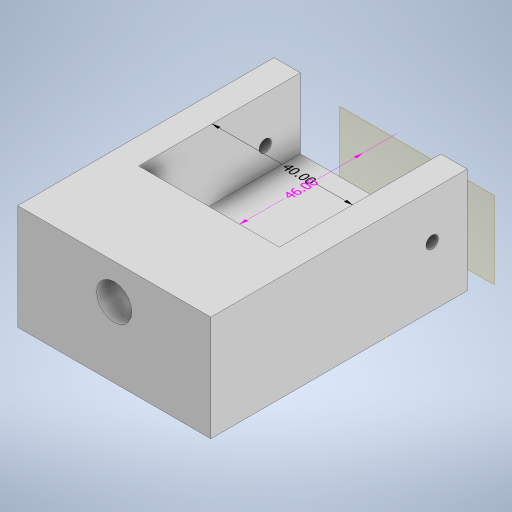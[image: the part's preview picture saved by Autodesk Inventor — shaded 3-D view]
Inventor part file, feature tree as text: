
AUTODESK INVENTOR PART (.ipt)
format: ipt  version: 2023 (Build 270158000, 158)  size: 300,544 bytes
history: native  units: mm
features: sketch x8, extrude x6, other x4, plane x3, hole x1, split x1
ambient origin geometry x8: Origin, YZ Plane, XZ Plane, XY Plane, X Axis, Y Axis, Z Axis, Center Point
bodies: Body1 (feature_tree)
feature tree (23):
  other  "Sólido1"
  other  "Anotaciones"
  extrude  "Extrusión1"  Depth=55.0mm
  extrude  "Extrusión2"  Depth=10.0mm
  extrude  "Extrusión3"  Depth=5.0mm
  extrude  "Extrusión4"  Depth=10.0mm TaperAngle=0.0deg
  plane  "Plano de trabajo1"
  extrude  "Extrusión5"  Depth=10.0mm
  plane  "Plano de trabajo2"
  extrude  "Extrusión6"  Depth=40.0mm
  sketch  "Boceto7"  dims[d15=46.0mm d16=20.0mm d17=0.0mm]
  plane  "Plano de trabajo4"
  hole  "Agujero1"  [1 undecoded]
  split  "Dividir1"
  sketch  "Boceto1"  dims[d0=55.0mm d1=100.0mm]
  sketch  "Boceto2"  dims[d2=30.0mm d3=0.0mm d4=10.0mm]
  sketch  "Boceto3"  dims[d5=20.0mm d6=5.0mm]
  sketch  "Boceto4"  dims[d7=22.5mm d8=10.0mm d9=0.0mm]
  sketch  "Boceto5"  dims[d10=10.0mm d11=10.0mm]
  sketch  "Boceto6"  dims[d12=15.0mm d13=0.0mm d14=40.0mm]
  sketch  "Boceto8"  dims[d24=22.5mm d25=2.5mm d26=2.5mm d27=8.0mm d28=0.0mm d29=3.0mm d30=3.0mm d31=8.0mm d32=0.0mm d33=0.0mm d34=10.0mm d35=30.0mm d36=5.0mm d37=5.0mm d38=5.0mm d39=5.0mm d40=10.0mm d41=8.0mm d42=3.5mm d43=6.0mm d44=4.0mm d45=2.0mm d46=90.0deg d47=8.0mm d48=20.594885mm d18=5.462798mm d19=4.90751mm d20=46.0mm d21=4.68859mm d22=6.124374mm d23=40.0mm]
  other  "Cota lineal 1"
  other  "Cota lineal 2"
note: 1 required parameter value undecoded (feature->parameter linkage not recoverable at this tier; creation-order binding heuristic only, values carry confidence <= 0.55)
